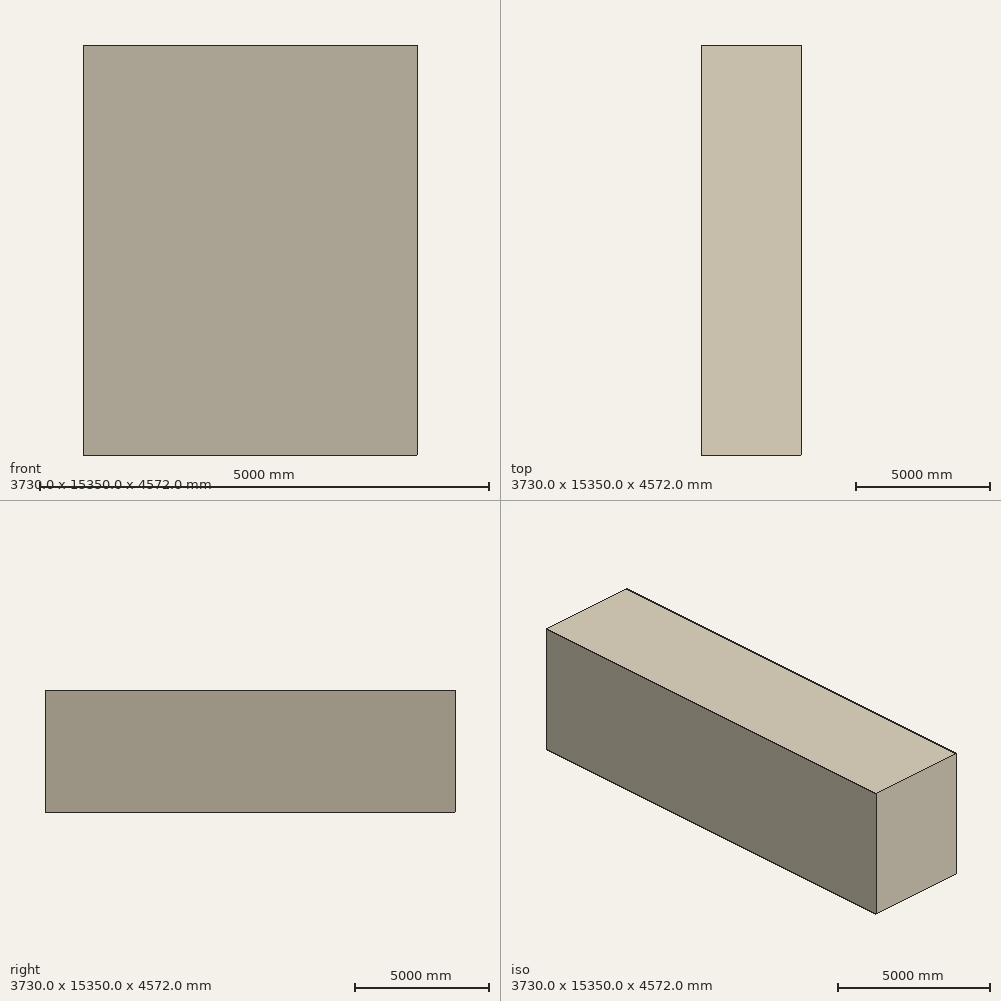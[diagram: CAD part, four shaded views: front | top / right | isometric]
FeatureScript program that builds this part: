
annotation { "Feature Type Name" : "Feature", "Feature Type Description" : "" }
export const myFeature = defineFeature(function(context is Context, id is Id, definition is map)
    precondition{}
    {
        {
            var Q0;
            Q0=qCreatedBy(makeId("Front.planeOp"),FACE);
            var sketch = newSketch(context, id + "F0", { "sketchPlane" : qUnion([Q0])});
            skLineSegment(sketch, "E0.bottom", {"start": v(-1866.47, 2659.57) * mm, "end": v(1863.53, 2659.57) * mm});
            skLineSegment(sketch, "E0.top", {"start": v(-1866.47, -1912.43) * mm, "end": v(1863.53, -1912.43) * mm});
            skLineSegment(sketch, "E0.left", {"start": v(-1866.47, 2659.57) * mm, "end": v(-1866.47, -1912.43) * mm});
            skLineSegment(sketch, "E0.right", {"start": v(1863.53, 2659.57) * mm, "end": v(1863.53, -1912.43) * mm});
            skSolve(sketch);
        }
        {
            var Q0;
            Q0 = qSketchRegion(id + "F0", true);
            extrude(context, id + "F1", {"entities" : qUnion([Q0]), "depth" : 15350 * mm});
        }
    });
